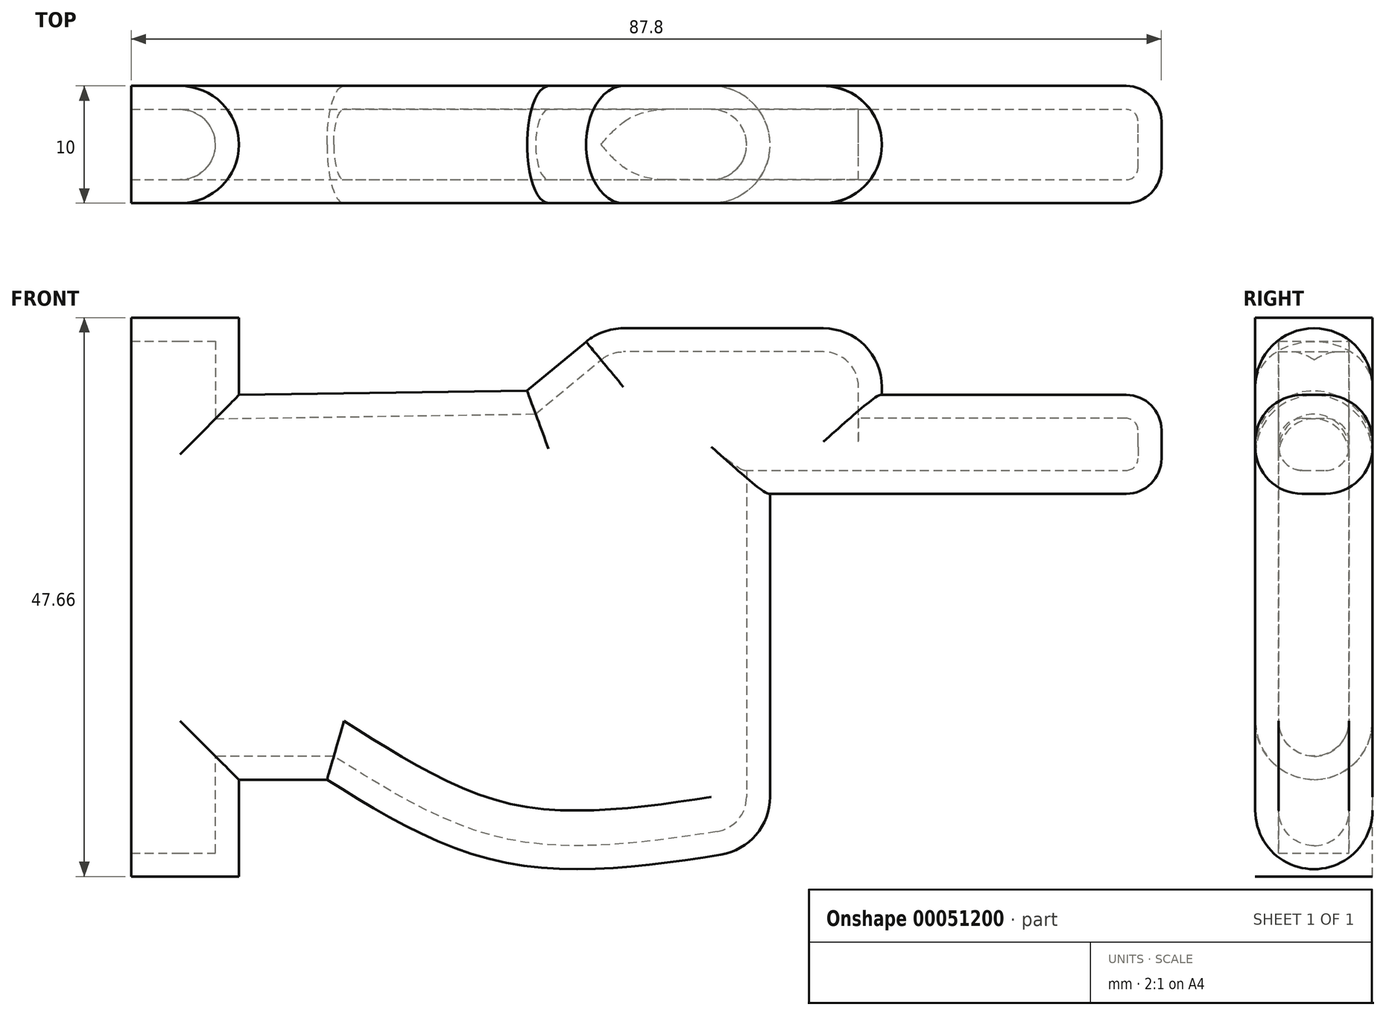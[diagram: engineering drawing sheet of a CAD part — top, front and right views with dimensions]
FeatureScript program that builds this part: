
annotation { "Feature Type Name" : "Feature", "Feature Type Description" : "" }
export const myFeature = defineFeature(function(context is Context, id is Id, definition is map)
    precondition{}
    {
        {
            var Q0;
            Q0=qCreatedBy(makeId("Front.planeOp"),FACE);
            var sketch = newSketch(context, id + "F0", { "sketchPlane" : qUnion([Q0])});
            skLineSegment(sketch, "E0", {"start": v(-56.46, 26.12) * mm, "end": v(-56.46, -21.54) * mm});
            skLineSegment(sketch, "E1", {"start": v(-56.46, -21.54) * mm, "end": v(-47.3, -21.54) * mm});
            skLineSegment(sketch, "E2", {"start": v(-56.46, 26.12) * mm, "end": v(-47.3, 26.12) * mm});
            skLineSegment(sketch, "E3", {"start": v(-47.3, 26.12) * mm, "end": v(-47.3, 19.52) * mm});
            skLineSegment(sketch, "E4", {"start": v(-47.3, -21.54) * mm, "end": v(-47.3, -13.29) * mm});
            skLineSegment(sketch, "E5", {"start": v(-47.3, -13.29) * mm, "end": v(-39.78, -13.29) * mm});
            skFitSpline(sketch, "E6", {"points": [v(-39.78, -13.29) * mm, v(-24.2, -20.44) * mm, v(-2.02, -18.97) * mm], "startDerivative": vector(31.37, -19.5) * mm, "endDerivative": vector(43.88, 7.56) * mm});
            skLineSegment(sketch, "E7", {"start": v(-2.02, -18.97) * mm, "end": v(-2.02, -12.92) * mm});
            skLineSegment(sketch, "E8", {"start": v(-2.02, -12.92) * mm, "end": v(-10.26, -12.92) * mm});
            skLineSegment(sketch, "E9", {"start": v(-2.02, -12.92) * mm, "end": v(-2.02, -6.14) * mm});
            skLineSegment(sketch, "E10", {"start": v(-2.02, -6.14) * mm, "end": v(-10.45, -6.14) * mm});
            skLineSegment(sketch, "E11", {"start": v(-2.02, -6.14) * mm, "end": v(-2.02, 2.47) * mm});
            skLineSegment(sketch, "E12", {"start": v(-2.02, 2.47) * mm, "end": v(-10.08, 2.47) * mm});
            skLineSegment(sketch, "E13", {"start": v(-2.02, 2.47) * mm, "end": v(-2.02, 11.09) * mm});
            skLineSegment(sketch, "E14", {"start": v(-2.02, 11.09) * mm, "end": v(-9.16, 11.09) * mm});
            skLineSegment(sketch, "E15", {"start": v(-2.02, 11.09) * mm, "end": v(31.34, 11.09) * mm});
            skLineSegment(sketch, "E16", {"start": v(31.34, 11.09) * mm, "end": v(31.34, 18.05) * mm});
            skLineSegment(sketch, "E17", {"start": v(31.34, 18.05) * mm, "end": v(31.34, 19.52) * mm});
            skLineSegment(sketch, "E18", {"start": v(31.34, 19.52) * mm, "end": v(7.52, 19.52) * mm});
            skLineSegment(sketch, "E19", {"start": v(7.52, 19.52) * mm, "end": v(7.52, 25.2) * mm});
            skLineSegment(sketch, "E20", {"start": v(7.52, 25.2) * mm, "end": v(-16.31, 25.2) * mm});
            skLineSegment(sketch, "E21", {"start": v(-16.31, 25.2) * mm, "end": v(-22.73, 19.89) * mm});
            skLineSegment(sketch, "E22", {"start": v(-22.73, 19.89) * mm, "end": v(-47.3, 19.52) * mm});
            skSolve(sketch);
        }
        {
            var Q0;
            Q0=makeQuery(id+"F0.imprint","IMPRINT",FACE,{"disambiguationData":[TD([[makeQuery(id+"F0.imprint","IMPRINT",EDGE,{"derivedFrom":sQuery(id+"F0.wireOp",EDGE,"E0")}),1.0]])]});
            extrude(context, id + "F1", {"entities" : qUnion([Q0]), "depth" : 10 * mm});
        }
        {
            var Q0;
            Q0=makeQuery(id+"F1.opExtrude","SWEPT_EDGE",EDGE,{"disambiguationData":[OSD([sQuery(id+"F0.wireOp",EDGE,"E6"),sQuery(id+"F0.wireOp",EDGE,"E7")])]});
            fillet(context, id + "F2", {"entities" : qUnion([Q0]), "radius" : 5 * mm, "tangentPropagation" : true, "allowEdgeOverflow" : false});
        }
        {
            var Q0;
            Q0=makeQuery(id+"F1.opExtrude","CAP_EDGE",EDGE,{"disambiguationData":[OSD([sQuery(id+"F0.wireOp",EDGE,"E16"),sQuery(id+"F0.wireOp",EDGE,"E17")])],"isStart":true});
            var Q1;
            Q1=makeQuery(id+"F1.opExtrude","SWEPT_EDGE",EDGE,{"disambiguationData":[OSD([sQuery(id+"F0.wireOp",EDGE,"E17"),sQuery(id+"F0.wireOp",EDGE,"E18")])]});
            var Q2;
            Q2=makeQuery(id+"F1.opExtrude","CAP_EDGE",EDGE,{"disambiguationData":[OSD([sQuery(id+"F0.wireOp",EDGE,"E16"),sQuery(id+"F0.wireOp",EDGE,"E17")])],"isStart":false});
            var Q3;
            Q3=makeQuery(id+"F1.opExtrude","SWEPT_EDGE",EDGE,{"disambiguationData":[OSD([sQuery(id+"F0.wireOp",EDGE,"E15"),sQuery(id+"F0.wireOp",EDGE,"E16")])]});
            fillet(context, id + "F3", {"entities" : qUnion([Q0, Q1, Q2, Q3]), "radius" : 3 * mm, "tangentPropagation" : true, "allowEdgeOverflow" : false});
        }
        {
            var Q0;
            Q0=makeQuery(id+"F1.opExtrude","CAP_EDGE",EDGE,{"disambiguationData":[OSD([sQuery(id+"F0.wireOp",EDGE,"E18")])],"isStart":false});
            var Q1;
            Q1=makeQuery(id+"F1.opExtrude","CAP_EDGE",EDGE,{"disambiguationData":[OSD([sQuery(id+"F0.wireOp",EDGE,"E18")])],"isStart":true});
            var Q2;
            Q2=makeQuery(id+"F1.opExtrude","CAP_EDGE",EDGE,{"disambiguationData":[OSD([sQuery(id+"F0.wireOp",EDGE,"E15")])],"isStart":true});
            var Q3;
            Q3=makeQuery(id+"F1.opExtrude","CAP_EDGE",EDGE,{"disambiguationData":[OSD([sQuery(id+"F0.wireOp",EDGE,"E15")])],"isStart":false});
            fillet(context, id + "F4", {"entities" : qUnion([Q0, Q1, Q2, Q3]), "radius" : 4 * mm, "tangentPropagation" : true, "allowEdgeOverflow" : false});
        }
        {
            var Q0;
            Q0=makeQuery(id+"F1.opExtrude","CAP_EDGE",EDGE,{"disambiguationData":[OSD([sQuery(id+"F0.wireOp",EDGE,"E22")])],"isStart":false});
            var Q1;
            Q1=makeQuery(id+"F1.opExtrude","CAP_EDGE",EDGE,{"disambiguationData":[OSD([sQuery(id+"F0.wireOp",EDGE,"E22")])],"isStart":true});
            var Q2;
            Q2=makeQuery(id+"F1.opExtrude","CAP_EDGE",EDGE,{"disambiguationData":[OSD([sQuery(id+"F0.wireOp",EDGE,"E3")])],"isStart":false});
            var Q3;
            Q3=makeQuery(id+"F1.opExtrude","CAP_EDGE",EDGE,{"disambiguationData":[OSD([sQuery(id+"F0.wireOp",EDGE,"E3")])],"isStart":true});
            var Q4;
            Q4=makeQuery(id+"F1.opExtrude","CAP_EDGE",EDGE,{"disambiguationData":[OSD([sQuery(id+"F0.wireOp",EDGE,"E4")])],"isStart":true});
            var Q5;
            Q5=makeQuery(id+"F1.opExtrude","CAP_EDGE",EDGE,{"disambiguationData":[OSD([sQuery(id+"F0.wireOp",EDGE,"E4")])],"isStart":false});
            var Q6;
            Q6=makeQuery(id+"F1.opExtrude","CAP_EDGE",EDGE,{"disambiguationData":[OSD([sQuery(id+"F0.wireOp",EDGE,"E7"),sQuery(id+"F0.wireOp",EDGE,"E9"),sQuery(id+"F0.wireOp",EDGE,"E11"),sQuery(id+"F0.wireOp",EDGE,"E13")])],"isStart":false});
            var Q7;
            Q7=makeQuery(id+"F1.opExtrude","CAP_EDGE",EDGE,{"disambiguationData":[OSD([sQuery(id+"F0.wireOp",EDGE,"E7"),sQuery(id+"F0.wireOp",EDGE,"E9"),sQuery(id+"F0.wireOp",EDGE,"E11"),sQuery(id+"F0.wireOp",EDGE,"E13")])],"isStart":true});
            fillet(context, id + "F5", {"entities" : qUnion([Q0, Q1, Q2, Q3, Q4, Q5, Q6, Q7]), "radius" : 5 * mm, "tangentPropagation" : true, "allowEdgeOverflow" : false});
        }
        {
            var Q0;
            Q0=makeQuery(id+"F1.opExtrude","CAP_EDGE",EDGE,{"disambiguationData":[OSD([sQuery(id+"F0.wireOp",EDGE,"E5")])],"isStart":false});
            var Q1;
            Q1=makeQuery(id+"F1.opExtrude","CAP_EDGE",EDGE,{"disambiguationData":[OSD([sQuery(id+"F0.wireOp",EDGE,"E5")])],"isStart":true});
            fillet(context, id + "F6", {"entities" : qUnion([Q0, Q1]), "radius" : 5 * mm, "tangentPropagation" : true, "allowEdgeOverflow" : false});
        }
        {
            var Q0;
            Q0=makeQuery(id+"F1.opExtrude","CAP_EDGE",EDGE,{"disambiguationData":[OSD([sQuery(id+"F0.wireOp",EDGE,"E21")])],"isStart":true});
            var Q1;
            Q1=makeQuery(id+"F1.opExtrude","CAP_EDGE",EDGE,{"disambiguationData":[OSD([sQuery(id+"F0.wireOp",EDGE,"E21")])],"isStart":false});
            var Q2;
            Q2=makeQuery(id+"F1.opExtrude","SWEPT_EDGE",EDGE,{"disambiguationData":[OSD([sQuery(id+"F0.wireOp",EDGE,"E20"),sQuery(id+"F0.wireOp",EDGE,"E21")])]});
            fillet(context, id + "F7", {"entities" : qUnion([Q0, Q1, Q2]), "radius" : 5 * mm, "tangentPropagation" : true, "allowEdgeOverflow" : false});
        }
        {
            var Q0;
            Q0=makeQuery(id+"F1.opExtrude","SWEPT_EDGE",EDGE,{"disambiguationData":[OSD([sQuery(id+"F0.wireOp",EDGE,"E19"),sQuery(id+"F0.wireOp",EDGE,"E20")])]});
            fillet(context, id + "F8", {"entities" : qUnion([Q0]), "radius" : 5 * mm, "tangentPropagation" : true, "allowEdgeOverflow" : false});
        }
        {
            var Q0;
            Q0=makeQuery(id+"F1.opExtrude","SWEPT_FACE",FACE,{"disambiguationData":[OSD([sQuery(id+"F0.wireOp",EDGE,"E0")])]});
            shell(context, id + "F9", {"entities" : qUnion([Q0]), "thickness" : 2 * mm});
        }
        {
            var Q0;
            Q0=makeQuery(id+"F1.opExtrude","CAP_EDGE",EDGE,{"disambiguationData":[OSD([sQuery(id+"F0.wireOp",EDGE,"E20")])],"isStart":true});
            var Q1;
            Q1=makeQuery(id+"F1.opExtrude","CAP_EDGE",EDGE,{"disambiguationData":[OSD([sQuery(id+"F0.wireOp",EDGE,"E20")])],"isStart":false});
            fillet(context, id + "F10", {"entities" : qUnion([Q0, Q1]), "radius" : 5 * mm, "tangentPropagation" : true, "allowEdgeOverflow" : false});
        }
    });
